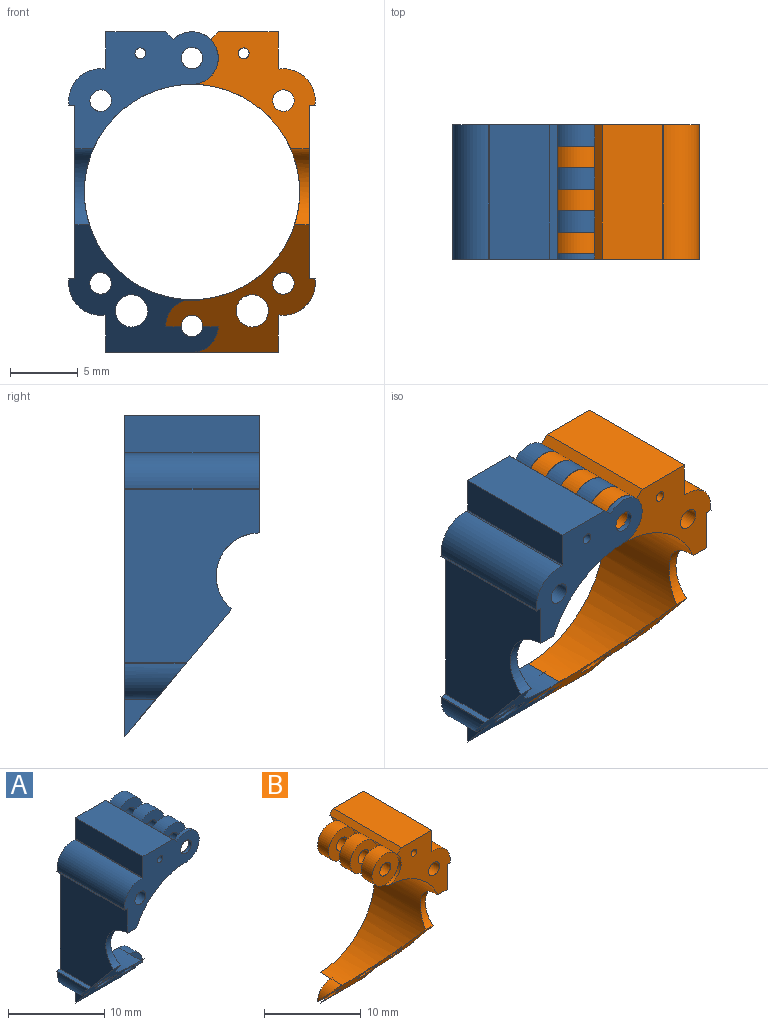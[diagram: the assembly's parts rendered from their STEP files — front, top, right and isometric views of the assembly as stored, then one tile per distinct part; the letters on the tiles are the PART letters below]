
ASSEMBLY  parts=2 mates=1
PART A: 45 faces, bbox 11.5x10.3x24 mm
  f0: plane 12.7x9.91mm, normal (-1,0,0), area 96.6mm2, adj f9,f10,f29,f42,f43,f44
  f1: cylinder r=1.94mm len=1.98mm, axis (0,1,0), area 2.9mm2, adj f2,f20,f23,f43
  f2: cylinder r=7.94mm len=15.88mm, axis (0,1,0), area 181.7mm2, adj f1,f19,f21,f22,f26,f27,f28,f29
  f3: plane 9.91x0.57mm, normal (0.71,0,0.71), area 8mm2, adj f4,f21,f26,f27,f28,f29,f30,f32
  f4: plane 9.91x4.41mm, normal (0,0,1), area 43.7mm2, adj f3,f5,f29,f42
  f5: plane 9.91x2.69mm, normal (-1,0,0), area 26.7mm2, adj f4,f6,f29,f42
  f6: cylinder r=11.11mm len=9.91mm, axis (0,1,0), area 0.9mm2, adj f5,f7,f29,f42
  f7: cylinder r=2.35mm len=9.91mm, axis (0,1,0), area 42.7mm2, adj f6,f8,f29,f42
  f8: cylinder r=11.11mm len=9.91mm, axis (0,1,0), area 0.9mm2, adj f7,f9,f29,f42
  f9: plane 9.91x0.48mm, normal (0,0,-1), area 4.8mm2, adj f0,f8,f29,f42
  f10: plane 4.58x0.48mm, normal (0,0,1), area 2.2mm2, adj f0,f11,f29,f43
  f11: cylinder r=11.11mm len=4.58mm, axis (0,1,0), area 0.4mm2, adj f10,f12,f29,f43
  f12: cylinder r=2.35mm len=4.52mm, axis (0,1,0), area 13.1mm2, adj f11,f13,f29,f43
  f13: cylinder r=11.11mm len=2.3mm, axis (0,1,0), area 0.2mm2, adj f12,f14,f29,f43
  f14: plane 2.69x2.26mm, normal (-1,0,0), area 3mm2, adj f13,f29,f43
  f15: cylinder r=0.8mm len=4.93mm, axis (0,1,0), area 21.5mm2, adj f29,f43
  f16: cylinder r=1.19mm len=3.56mm, axis (0,1,0), area 19.4mm2, adj f29,f43
  f17: cylinder r=0.4mm len=9.91mm, axis (0,1,0), area 24.7mm2, adj f29,f42
  f18: cylinder r=0.79mm len=9.91mm, axis (0,1,0), area 49.4mm2, adj f29,f42
  f19: cylinder r=1.94mm len=3.87mm, axis (0,1,0), area 6.6mm2, adj f2,f20,f29,f43
  f20: plane 3.87x1.98mm, normal (0,-1,0), area 5mm2, adj f1,f19,f25,f43
  f21: cylinder r=1.94mm len=3.87mm, axis (0,1,0), area 2.9mm2, adj f2,f3,f38,f42
  f22: cylinder r=1.94mm len=0.58mm, axis (0,1,0), area 0mm2, adj f2,f23,f43
  f23: plane 1.17x0.09mm, normal (0,1,0), area 0.1mm2, adj f1,f22,f43
  f24: cylinder r=0.79mm len=1.59mm, axis (0,1,0), area 1.9mm2, adj f38,f42
  f25: cylinder r=0.79mm len=1.59mm, axis (0,1,0), area 7mm2, adj f20,f29,f43
  f26: cylinder r=1.94mm len=3.31mm, axis (0,1,0), area 7.2mm2, adj f2,f3,f36,f38
  f27: cylinder r=1.94mm len=3.31mm, axis (0,1,0), area 7.2mm2, adj f2,f3,f33,f37
  f28: cylinder r=1.94mm len=3.31mm, axis (0,1,0), area 7.2mm2, adj f2,f3,f31,f34
  f29: plane 23.62x11.06mm, normal (0,1,0), area 91.1mm2, adj f0,f2,f3,f4,f5,f6,f7,f8
  f30: cylinder r=1.94mm len=3.87mm, axis (0,1,0), area 12.1mm2, adj f2,f3,f29,f31
  f31: plane 3.87x3.87mm, normal (0,-1,0), area 9.8mm2, adj f28,f30,f41
  f32: cylinder r=1.94mm len=3.87mm, axis (0,1,0), area 12.1mm2, adj f2,f3,f33,f34
  f33: plane 3.87x3.87mm, normal (0,-1,0), area 9.8mm2, adj f27,f32,f40
  f34: plane 3.87x3.87mm, normal (0,1,0), area 9.8mm2, adj f28,f32,f40
  f35: cylinder r=1.94mm len=3.87mm, axis (0,1,0), area 12.1mm2, adj f2,f3,f36,f37
  f36: plane 3.87x3.87mm, normal (0,-1,0), area 9.8mm2, adj f26,f35,f39
  f37: plane 3.87x3.87mm, normal (0,1,0), area 9.8mm2, adj f27,f35,f39
  f38: plane 3.87x3.87mm, normal (0,1,0), area 9.8mm2, adj f21,f24,f26
  f39: cylinder r=0.79mm len=1.59mm, axis (0,1,0), area 7.9mm2, adj f36,f37
  f40: cylinder r=0.79mm len=1.59mm, axis (0,1,0), area 7.9mm2, adj f33,f34
  f41: cylinder r=0.79mm len=1.59mm, axis (0,1,0), area 7.9mm2, adj f29,f31
  f42: plane 11.06x8.64mm, normal (0,-1,0), area 44.5mm2, adj f0,f2,f3,f4,f5,f6,f7,f8
  f43: plane 11.48x9.8mm, normal (0,-0.77,-0.64), area 48.1mm2, adj f0,f1,f2,f10,f11,f12,f13,f14
  f44: cylinder r=3.17mm len=5.61mm, axis (-1,0,0), area 7.4mm2, adj f0,f2,f42,f43
PART B: 44 faces, bbox 11.5x10.3x24 mm
  f0: plane 12.7x9.91mm, normal (1,0,0), area 96.6mm2, adj f16,f17,f24,f41,f42,f43
  f1: cylinder r=1.94mm len=0.58mm, axis (0,-1,0), area 0mm2, adj f11,f29,f42
  f2: cylinder r=1.94mm len=3.31mm, axis (0,-1,0), area 1.8mm2, adj f10,f11,f35,f41
  f3: cylinder r=1.94mm len=3.31mm, axis (0,-1,0), area 7.2mm2, adj f10,f11,f32,f36
  f4: cylinder r=1.94mm len=3.31mm, axis (0,-1,0), area 7.2mm2, adj f10,f11,f26,f33
  f5: cylinder r=1.94mm len=3.87mm, axis (0,-1,0), area 6.6mm2, adj f11,f24,f30,f42
  f6: cylinder r=1.94mm len=3.31mm, axis (0,-1,0), area 7.2mm2, adj f10,f11,f24,f27
  f7: cylinder r=11.11mm len=9.91mm, axis (0,-1,0), area 0.9mm2, adj f8,f21,f24,f41
  f8: plane 9.91x2.69mm, normal (1,0,0), area 26.7mm2, adj f7,f9,f24,f41
  f9: plane 9.91x4.41mm, normal (0,0,1), area 43.7mm2, adj f8,f10,f24,f41
  f10: plane 9.91x0.57mm, normal (-0.71,0,0.71), area 8mm2, adj f2,f3,f4,f6,f9,f24,f25,f31
  f11: cylinder r=7.94mm len=15.88mm, axis (0,-1,0), area 181.7mm2, adj f1,f2,f3,f4,f5,f6,f24,f25
  f12: plane 2.69x2.26mm, normal (1,0,0), area 3mm2, adj f13,f24,f42
  f13: cylinder r=11.11mm len=2.3mm, axis (0,-1,0), area 0.2mm2, adj f12,f14,f24,f42
  f14: cylinder r=2.35mm len=4.52mm, axis (0,-1,0), area 13.1mm2, adj f13,f15,f24,f42
  f15: cylinder r=11.11mm len=4.58mm, axis (0,-1,0), area 0.4mm2, adj f14,f16,f24,f42
  f16: plane 4.58x0.48mm, normal (0,0,1), area 2.2mm2, adj f0,f15,f24,f42
  f17: plane 9.91x0.48mm, normal (0,0,-1), area 4.8mm2, adj f0,f18,f24,f41
  f18: cylinder r=11.11mm len=9.91mm, axis (0,-1,0), area 0.9mm2, adj f17,f21,f24,f41
  f19: cylinder r=0.79mm len=4.93mm, axis (0,-1,0), area 21.1mm2, adj f24,f42
  f20: cylinder r=1.19mm len=3.56mm, axis (0,-1,0), area 18.9mm2, adj f24,f42
  f21: cylinder r=2.35mm len=9.91mm, axis (0,-1,0), area 42.7mm2, adj f7,f18,f24,f41
  f22: cylinder r=0.4mm len=9.91mm, axis (0,-1,0), area 24.7mm2, adj f24,f41
  f23: cylinder r=0.79mm len=9.91mm, axis (0,-1,0), area 49.4mm2, adj f24,f41
  f24: plane 23.62x9.12mm, normal (0,1,0), area 71.6mm2, adj f0,f5,f6,f7,f8,f9,f10,f11
  f25: cylinder r=1.94mm len=3.87mm, axis (0,1,0), area 12.1mm2, adj f10,f11,f26,f27
  f26: plane 3.87x3.87mm, normal (0,-1,0), area 9.8mm2, adj f4,f25,f39
  f27: plane 3.87x3.87mm, normal (0,1,0), area 9.8mm2, adj f6,f25,f39
  f28: cylinder r=1.94mm len=1.98mm, axis (0,1,0), area 2.9mm2, adj f11,f29,f30,f42
  f29: plane 1.17x0.09mm, normal (0,-1,0), area 0.1mm2, adj f1,f28,f42
  f30: plane 3.87x1.98mm, normal (0,1,0), area 5mm2, adj f5,f28,f40,f42
  f31: cylinder r=1.94mm len=3.87mm, axis (0,1,0), area 12.1mm2, adj f10,f11,f32,f33
  f32: plane 3.87x3.87mm, normal (0,-1,0), area 9.8mm2, adj f3,f31,f38
  f33: plane 3.87x3.87mm, normal (0,1,0), area 9.8mm2, adj f4,f31,f38
  f34: cylinder r=1.94mm len=3.87mm, axis (0,1,0), area 12.1mm2, adj f10,f11,f35,f36
  f35: plane 3.87x3.87mm, normal (0,-1,0), area 9.8mm2, adj f2,f34,f37
  f36: plane 3.87x3.87mm, normal (0,1,0), area 9.8mm2, adj f3,f34,f37
  f37: cylinder r=0.79mm len=1.59mm, axis (0,1,0), area 7.9mm2, adj f35,f36
  f38: cylinder r=0.79mm len=1.59mm, axis (0,1,0), area 7.9mm2, adj f32,f33
  f39: cylinder r=0.79mm len=1.59mm, axis (0,1,0), area 7.9mm2, adj f26,f27
  f40: cylinder r=0.79mm len=1.59mm, axis (0,1,0), area 1.2mm2, adj f30,f42
  f41: plane 9.12x8.64mm, normal (0,-1,0), area 34.6mm2, adj f0,f2,f7,f8,f9,f10,f11,f17
  f42: plane 11.48x9.8mm, normal (0,-0.77,-0.64), area 48.2mm2, adj f0,f1,f5,f11,f12,f13,f14,f15
  f43: cylinder r=3.17mm len=5.61mm, axis (1,0,0), area 7.4mm2, adj f0,f11,f41,f42
PLACE A t=(-8.49,-2.64,-0.76)mm
PLACE B rot(axis=(0,1,0),0deg) t=(-4.92,-28.04,8.28)mm
MATE revolute B.f2 <-> A.f21  axis (0,1,0) through (-7.53,-4.23,8.34)mm
